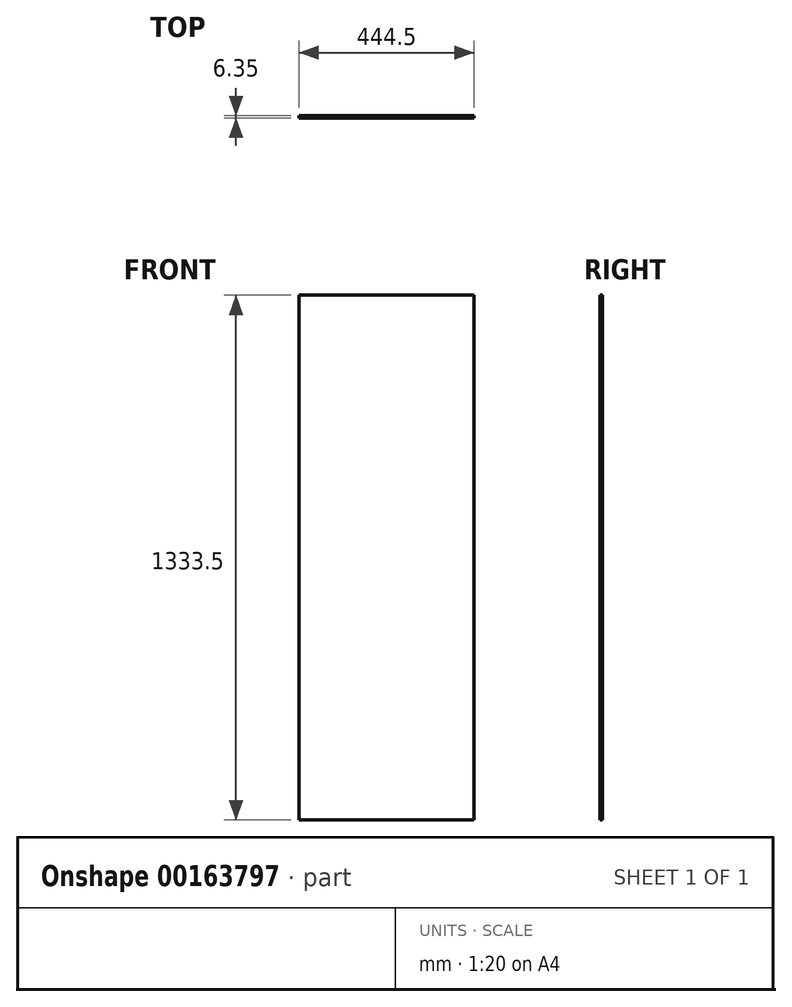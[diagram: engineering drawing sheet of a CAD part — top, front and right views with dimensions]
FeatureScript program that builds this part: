
annotation { "Feature Type Name" : "Feature", "Feature Type Description" : "" }
export const myFeature = defineFeature(function(context is Context, id is Id, definition is map)
    precondition{}
    {
        {
            var Q0;
            Q0=qCreatedBy(makeId("Front.planeOp"),FACE);
            var sketch = newSketch(context, id + "F0", { "sketchPlane" : qUnion([Q0])});
            skLineSegment(sketch, "E0.bottom", {"start": v(-222.25, -666.75) * mm, "end": v(222.25, -666.75) * mm});
            skLineSegment(sketch, "E0.top", {"start": v(-222.25, 666.75) * mm, "end": v(222.25, 666.75) * mm});
            skLineSegment(sketch, "E0.left", {"start": v(-222.25, -666.75) * mm, "end": v(-222.25, 666.75) * mm});
            skLineSegment(sketch, "E0.right", {"start": v(222.25, -666.75) * mm, "end": v(222.25, 666.75) * mm});
            skPoint(sketch, "E0.middle", {"position": v(0, 0) * mm});
            skSolve(sketch);
        }
        {
            var Q0;
            Q0 = qSketchRegion(id + "F0", true);
            extrude(context, id + "F1", {"entities" : qUnion([Q0]), "depth" : 6.35 * mm});
        }
    });
